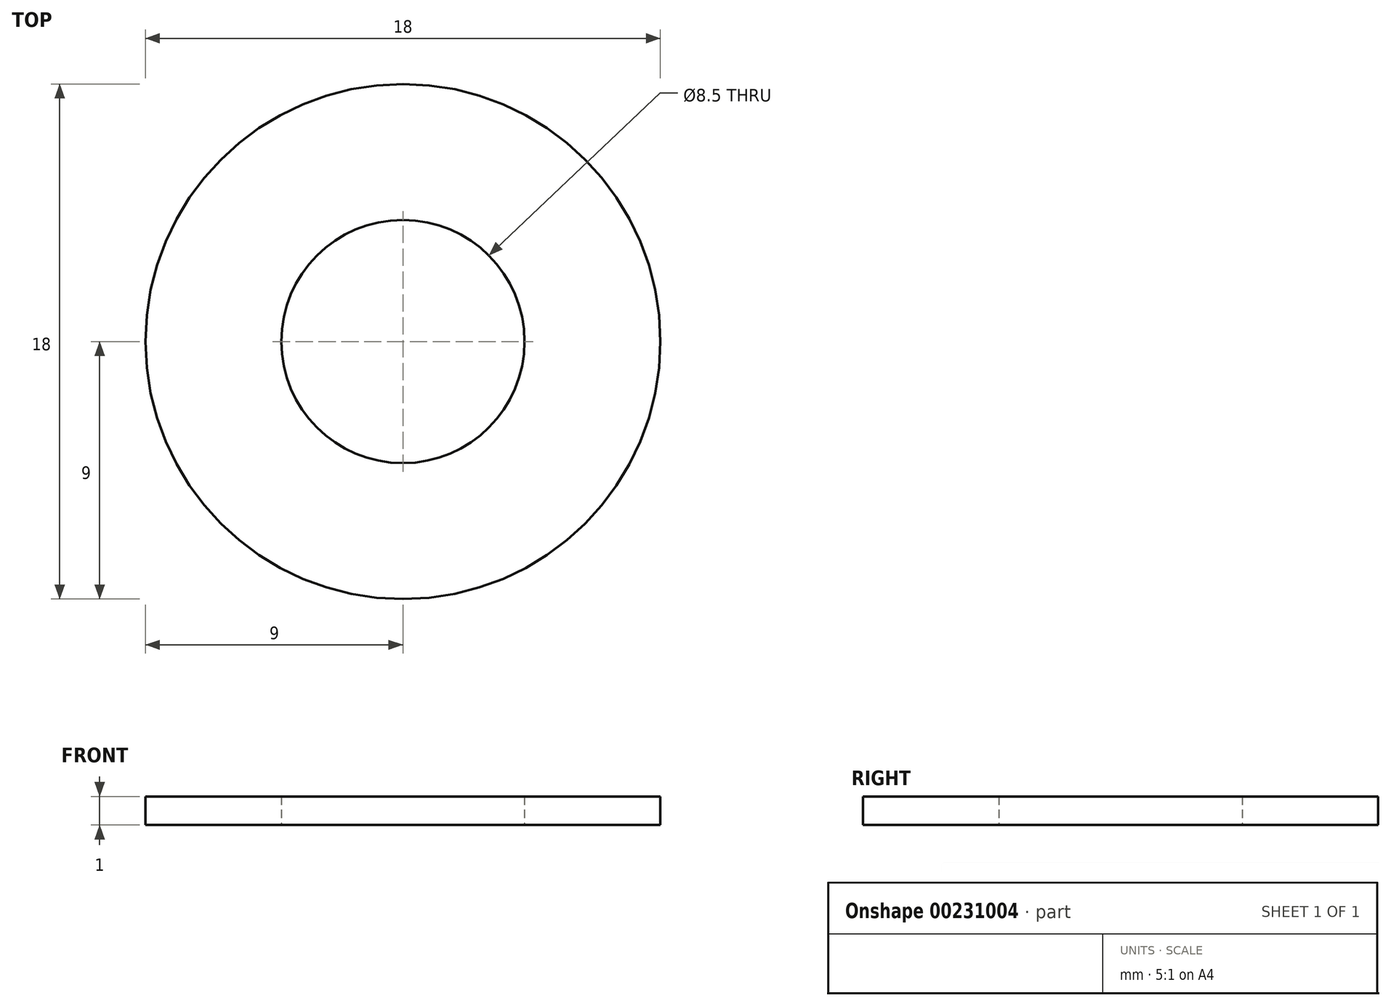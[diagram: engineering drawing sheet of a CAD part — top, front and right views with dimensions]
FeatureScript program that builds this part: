
annotation { "Feature Type Name" : "Feature", "Feature Type Description" : "" }
export const myFeature = defineFeature(function(context is Context, id is Id, definition is map)
    precondition{}
    {
        {
            var Q0;
            Q0=qCreatedBy(makeId("Top.planeOp"),FACE);
            var sketch = newSketch(context, id + "F0", { "sketchPlane" : qUnion([Q0])});
            skCircle(sketch, "E0", {"center": v(0, 0) * mm, "radius": 4.25 * mm});
            skCircle(sketch, "E1", {"center": v(0, 0) * mm, "radius": 9 * mm});
            skSolve(sketch);
        }
        {
            var Q0;
            Q0=makeQuery(id+"F0.imprint","IMPRINT",FACE,{"disambiguationData":[TD([[makeQuery(id+"F0.imprint","IMPRINT",EDGE,{"derivedFrom":sQuery(id+"F0.wireOp",EDGE,"E0")}),-1.0]])]});
            extrude(context, id + "F1", {"entities" : qUnion([Q0]), "depth" : 1 * mm});
        }
    });
